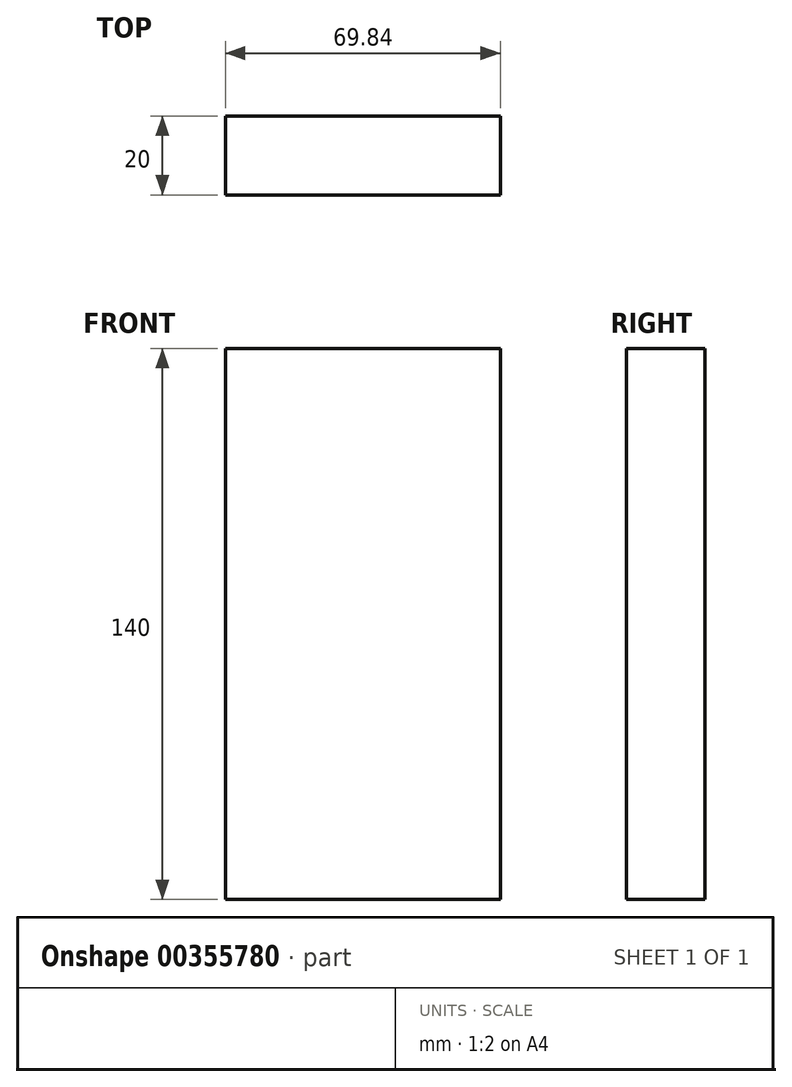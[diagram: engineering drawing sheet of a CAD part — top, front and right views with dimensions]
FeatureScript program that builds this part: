
annotation { "Feature Type Name" : "Feature", "Feature Type Description" : "" }
export const myFeature = defineFeature(function(context is Context, id is Id, definition is map)
    precondition{}
    {
        {
            var Q0;
            Q0=qCreatedBy(makeId("Front.planeOp"),FACE);
            var sketch = newSketch(context, id + "F0", { "sketchPlane" : qUnion([Q0])});
            skLineSegment(sketch, "E0", {"start": v(0, 0) * mm, "end": v(-34.93, 0) * mm, "construction": true});
            skLineSegment(sketch, "E1", {"start": v(0, 0) * mm, "end": v(34.93, 0) * mm, "construction": true});
            skLineSegment(sketch, "E2", {"start": v(0, 0) * mm, "end": v(0, 140) * mm, "construction": true});
            skLineSegment(sketch, "E3", {"start": v(-34.93, 0) * mm, "end": v(-34.93, 140) * mm});
            skLineSegment(sketch, "E4", {"start": v(-34.93, 140) * mm, "end": v(34.93, 140) * mm});
            skLineSegment(sketch, "E5", {"start": v(34.93, 140) * mm, "end": v(34.93, 0) * mm});
            skLineSegment(sketch, "E6", {"start": v(34.93, 0) * mm, "end": v(-34.93, 0) * mm});
            skSolve(sketch);
        }
        {
            var Q0;
            Q0=makeQuery(id+"F0.imprint","IMPRINT",FACE,{"disambiguationData":[TD([[makeQuery(id+"F0.imprint","IMPRINT",EDGE,{"derivedFrom":sQuery(id+"F0.wireOp",EDGE,"E3")}),-1.0]])]});
            extrude(context, id + "F1", {"entities" : qUnion([Q0]), "endBound" : BoundingType.SYMMETRIC, "oppositeDirection" : true, "depth" : 20 * mm});
        }
        {
            var Q0;
            Q0=makeQuery(id+"F1.opExtrude","SWEPT_FACE",FACE,{"disambiguationData":[OSD([sQuery(id+"F0.wireOp",EDGE,"E5")])]});
            cPlane(context, id + "F2", {"entities" : qUnion([Q0]), "cplaneType" : CPlaneType.OFFSET, "offset" : 0 * mm, "width" : 152.4 * mm, "height" : 152.4 * mm});
        }
    });
